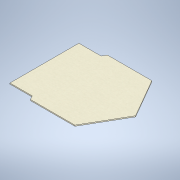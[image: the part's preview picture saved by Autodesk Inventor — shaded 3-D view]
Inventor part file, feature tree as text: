
AUTODESK INVENTOR PART (.ipt)
format: ipt  version: 2021 (Build 250183000, 183)  size: 110,592 bytes
history: native  units: mm
features: extrude x1, sketch x1
ambient origin geometry x8: Origin, YZ Plane, XZ Plane, XY Plane, X Axis, Y Axis, Z Axis, Center Point
bodies: Solid1 (feature_tree)
feature tree (2):
  extrude  "Extrusion1"  Depth=191.0mm
  sketch  "Sketch1"  dims[d3=2.55mm d4=0.0mm d5=191.0mm d6=171.0mm d7=116.0mm]
